# Revit family: Vela Galvanised – Cast In Place
name_source: partatom
category: Furniture
units: mm (PartAtom-declared; Revit-internal decimal feet)

## family parameters
Always vertical = Yes
Cut with Voids When Loaded = No
OmniClass Number = 23.21.23.13.15
Room Calculation Point = No
Shared = No
Work Plane-Based = No

## types (2) — shared parameters
Body material = Hags - Steel - Galvanized
Body material_90 = Hags - Steel - Galvanized
Construction material = Hags - Steel - Galvanized
Description = Sofa Sofiero Detached
Edition number = 1
Manufacturer = Hags
Manufacturer name = HAGS
OmniClass Code = 23-21 23 13 15
Product Guid = 90e49432-c870-4a59-897e-b15016e8f9bd
Product data url = https://bimobject.com
Product url = https://hags.se
QR code = https://www.hags.com
URL = https://www.hags.com
Uniclass 1.4 Code = L8211
Uniclass 1.4 Description = Furniture
zero-valued in all types: Default Elevation

## per-type parameters (varying)
| type | BIMobject category | IFC Classification | Model | OmniClass Description | Product SKU | Product name |
| 8012596 / Galvanized | PARK AND URBAN FURNITURE | FURNITURE | 8037012 | BICYCLE STORAGE | Vella_Detached | Vela Galvanised – Cast In Place |
| 8037716 / Galvanized | Bench & Park Bench | Furniture | 8037014 | Residential Sofas | Table_Ekeby_Detached | Ekeby Table Cast In Place |

## geometry (parser evidence)
native form markers: Sweep x2
no freeform markers — native parametric forms only
